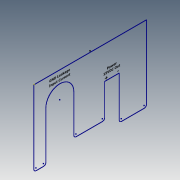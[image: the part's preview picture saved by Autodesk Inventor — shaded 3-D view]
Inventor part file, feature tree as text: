
AUTODESK INVENTOR PART (.ipt)
format: ipt  version: 2020.5 (Build 245400000, 400)  size: 132,608 bytes
history: native  units: mm
features: sketch x1
ambient origin geometry x8: Origin, YZ Plane, XZ Plane, XY Plane, X Axis, Y Axis, Z Axis, Center Point
feature tree (1):
  sketch  "Sketch30"  dims[d13=18.0mm d14=60.0mm d660=2.7mm d661=19.1mm d662=2.7mm d663=18.6mm d664=36.361013mm d665=4.351086mm d666=36.611013mm d667=8.051086mm d668=2.1mm d669=8.9mm d670=2.1mm d671=15.2mm d672=0.599999mm d673=1.799998mm d674=2.599986mm d675=3.299982mm d676=26.905472mm d677=12.841302mm d678=23.305472mm d679=11.859893mm d680=20.205472mm d681=15.009893mm d682=27.89455mm d683=24.218985mm]
